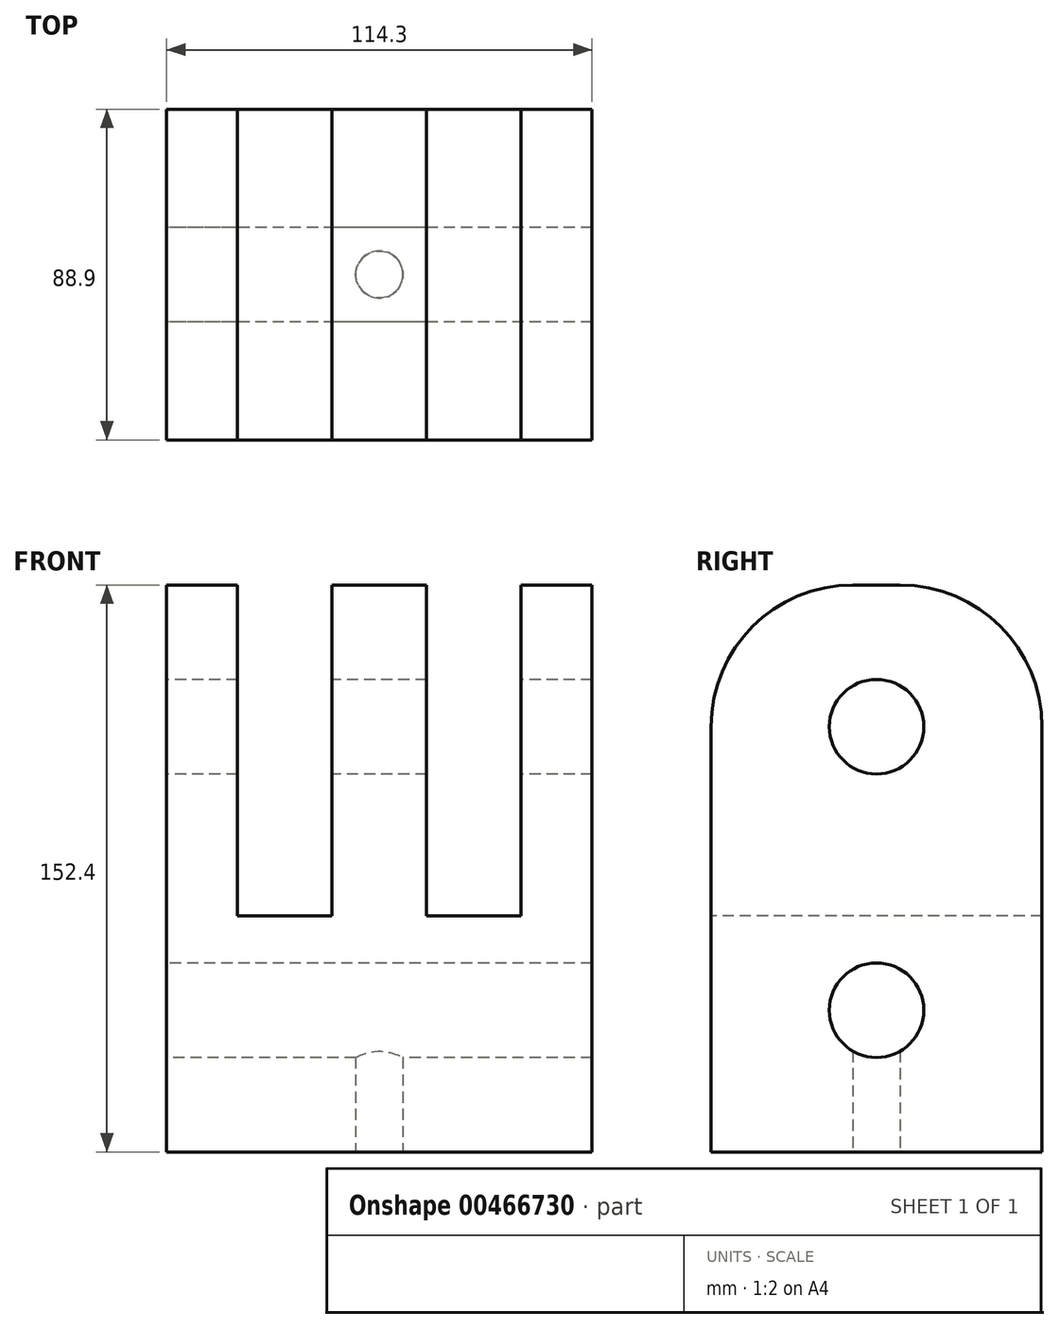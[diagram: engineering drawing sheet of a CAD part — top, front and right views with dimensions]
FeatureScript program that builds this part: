
annotation { "Feature Type Name" : "Feature", "Feature Type Description" : "" }
export const myFeature = defineFeature(function(context is Context, id is Id, definition is map)
    precondition{}
    {
        {
            var Q0;
            Q0=qCreatedBy(makeId("Top.planeOp"),FACE);
            var sketch = newSketch(context, id + "F0", { "sketchPlane" : qUnion([Q0])});
            skLineSegment(sketch, "E0.bottom", {"start": v(57.15, -44.45) * mm, "end": v(-57.15, -44.45) * mm});
            skLineSegment(sketch, "E0.top", {"start": v(57.15, 44.45) * mm, "end": v(-57.15, 44.45) * mm});
            skLineSegment(sketch, "E0.left", {"start": v(57.15, -44.45) * mm, "end": v(57.15, 44.45) * mm});
            skLineSegment(sketch, "E0.right", {"start": v(-57.15, -44.45) * mm, "end": v(-57.15, 44.45) * mm});
            skPoint(sketch, "E0.middle", {"position": v(0, 0) * mm});
            skSolve(sketch);
        }
        {
            var Q0;
            Q0 = qSketchRegion(id + "F0", true);
            extrude(context, id + "F1", {"entities" : qUnion([Q0]), "depth" : 152.4 * mm});
        }
        {
            var Q0;
            Q0=makeQuery(id+"F1.opExtrude","SWEPT_FACE",FACE,{"disambiguationData":[OSD([sQuery(id+"F0.wireOp",EDGE,"E0.bottom")])]});
            var sketch = newSketch(context, id + "F2", { "sketchPlane" : qUnion([Q0])});
            skLineSegment(sketch, "E1.top", {"start": v(38.1, 63.5) * mm, "end": v(12.7, 63.5) * mm});
            skLineSegment(sketch, "E1.left", {"start": v(38.1, 152.4) * mm, "end": v(38.1, 63.5) * mm});
            skLineSegment(sketch, "E2.bottom", {"start": v(-12.7, 152.4) * mm, "end": v(-38.1, 152.4) * mm});
            skLineSegment(sketch, "E2.top", {"start": v(-12.7, 63.5) * mm, "end": v(-38.1, 63.5) * mm});
            skLineSegment(sketch, "E2.left", {"start": v(-12.7, 152.4) * mm, "end": v(-12.7, 63.5) * mm});
            skLineSegment(sketch, "E2.right", {"start": v(-38.1, 152.4) * mm, "end": v(-38.1, 63.5) * mm});
            skLineSegment(sketch, "E3", {"start": v(12.7, 152.4) * mm, "end": v(12.7, 63.5) * mm});
            skSolve(sketch);
        }
        {
            var Q0;
            Q0 = qSketchRegion(id + "F2", true);
            var Q1;
            Q1=makeQuery(id+"F2.imprint","IMPRINT",FACE,{"disambiguationData":[TD([[makeQuery(id+"F2.imprint","IMPRINT",EDGE,{"derivedFrom":sQuery(id+"F2.wireOp",EDGE,"E1.top")}),-1.0]])]});
            extrude(context, id + "F3", {"entities" : qUnion([Q0, Q1]), "operationType" : NewBodyOperationType.REMOVE, "endBound" : BoundingType.THROUGH_ALL, "oppositeDirection" : true, "depth" : 25.4 * mm});
        }
        {
            var Q0;
            {var subQ0=sQuery(id+"F0.wireOp",EDGE,"E0.bottom");var subQ1=sQuery(id+"F0.wireOp",EDGE,"E0.left");Q0=makeQuery(id+"F3.boolean.opBoolean","SPLIT",EDGE,{"disambiguationData":[TD([makeQuery(id+"F1.opExtrude","SWEPT_FACE",FACE,{"disambiguationData":[OSD([subQ1])]})])],"derivedFrom":makeQuery(id+"F1.opExtrude","CAP_EDGE",EDGE,{"disambiguationData":[OSD([subQ0])],"isStart":false})});}
            var Q1;
            {var subQ0=sQuery(id+"F0.wireOp",EDGE,"E0.bottom");Q1=makeQuery(id+"F3.boolean.opBoolean","SPLIT",EDGE,{"disambiguationData":[TD([makeQuery(id+"F3.opExtrude","SWEPT_FACE",FACE,{"disambiguationData":[OSD([sQuery(id+"F2.wireOp",EDGE,"E2.left")])]})])],"derivedFrom":makeQuery(id+"F1.opExtrude","CAP_EDGE",EDGE,{"disambiguationData":[OSD([subQ0])],"isStart":false})});}
            var Q2;
            {var subQ0=sQuery(id+"F0.wireOp",EDGE,"E0.bottom");var subQ1=sQuery(id+"F0.wireOp",EDGE,"E0.right");Q2=makeQuery(id+"F3.boolean.opBoolean","SPLIT",EDGE,{"disambiguationData":[TD([makeQuery(id+"F1.opExtrude","SWEPT_FACE",FACE,{"disambiguationData":[OSD([subQ1])]})])],"derivedFrom":makeQuery(id+"F1.opExtrude","CAP_EDGE",EDGE,{"disambiguationData":[OSD([subQ0])],"isStart":false})});}
            var Q3;
            {var subQ0=sQuery(id+"F0.wireOp",EDGE,"E0.right");var subQ1=sQuery(id+"F0.wireOp",EDGE,"E0.top");Q3=makeQuery(id+"F3.boolean.opBoolean","SPLIT",EDGE,{"disambiguationData":[TD([makeQuery(id+"F1.opExtrude","SWEPT_FACE",FACE,{"disambiguationData":[OSD([subQ0])]})])],"derivedFrom":makeQuery(id+"F1.opExtrude","CAP_EDGE",EDGE,{"disambiguationData":[OSD([subQ1])],"isStart":false})});}
            var Q4;
            {var subQ0=sQuery(id+"F0.wireOp",EDGE,"E0.top");Q4=makeQuery(id+"F3.boolean.opBoolean","SPLIT",EDGE,{"disambiguationData":[TD([makeQuery(id+"F3.opExtrude","SWEPT_FACE",FACE,{"disambiguationData":[OSD([sQuery(id+"F2.wireOp",EDGE,"E2.left")])]})])],"derivedFrom":makeQuery(id+"F1.opExtrude","CAP_EDGE",EDGE,{"disambiguationData":[OSD([subQ0])],"isStart":false})});}
            var Q5;
            {var subQ0=sQuery(id+"F0.wireOp",EDGE,"E0.left");var subQ1=sQuery(id+"F0.wireOp",EDGE,"E0.top");Q5=makeQuery(id+"F3.boolean.opBoolean","SPLIT",EDGE,{"disambiguationData":[TD([makeQuery(id+"F1.opExtrude","SWEPT_FACE",FACE,{"disambiguationData":[OSD([subQ0])]})])],"derivedFrom":makeQuery(id+"F1.opExtrude","CAP_EDGE",EDGE,{"disambiguationData":[OSD([subQ1])],"isStart":false})});}
            fillet(context, id + "F4", {"entities" : qUnion([Q0, Q1, Q2, Q3, Q4, Q5]), "radius" : 38.1 * mm, "tangentPropagation" : true, "allowEdgeOverflow" : false});
        }
        {
            var Q0;
            Q0=makeQuery(id+"F1.opExtrude","SWEPT_FACE",FACE,{"disambiguationData":[OSD([sQuery(id+"F0.wireOp",EDGE,"E0.right")])]});
            var sketch = newSketch(context, id + "F5", { "sketchPlane" : qUnion([Q0])});
            skCircle(sketch, "E4", {"center": v(0, 38.1) * mm, "radius": 12.7 * mm});
            skCircle(sketch, "E5", {"center": v(0, 114.3) * mm, "radius": 12.7 * mm});
            skSolve(sketch);
        }
        {
            var Q0;
            Q0 = qSketchRegion(id + "F5", true);
            extrude(context, id + "F6", {"entities" : qUnion([Q0]), "operationType" : NewBodyOperationType.REMOVE, "endBound" : BoundingType.THROUGH_ALL, "oppositeDirection" : true, "depth" : 25.4 * mm});
        }
        {
            var Q0;
            Q0=makeQuery(id+"F1.opExtrude","CAP_FACE",FACE,{"disambiguationData":[OSD([sQuery(id+"F0.wireOp",EDGE,"E0.bottom"),sQuery(id+"F0.wireOp",EDGE,"E0.top"),sQuery(id+"F0.wireOp",EDGE,"E0.left"),sQuery(id+"F0.wireOp",EDGE,"E0.right")])],"isStart":true});
            var sketch = newSketch(context, id + "F7", { "sketchPlane" : qUnion([Q0])});
            skCircle(sketch, "E6", {"center": v(0, 0) * mm, "radius": 6.35 * mm});
            skSolve(sketch);
        }
        {
            var Q0;
            Q0 = qSketchRegion(id + "F7", true);
            extrude(context, id + "F8", {"entities" : qUnion([Q0]), "operationType" : NewBodyOperationType.REMOVE, "oppositeDirection" : true, "depth" : 38.1 * mm});
        }
    });
